# Revit family: Varmax_525_600_2-3Piquages - depuis 2020-06_FR_#
name_source: partatom
category: Equipement de génie climatique
revit_build: Autodesk Revit 2016 (Build: 20150220_1215(x64)
units: mm (PartAtom-declared; Revit-internal decimal feet)

## family parameters
Basée sur le plan de construction = Non
Cote de connecteur circulaire = Utiliser le diamètre
Couper avec des vides une fois chargée = Non
Numéro OmniClass = 23.75.00.00
Partagée = Non
Point de calcul de pièce = Oui
Titre OmniClass = Climate Control (HVAC)
Toujours verticalement = Oui
Type d'élément = Normal

## types (6) — shared parameters
Classe Nox = 6
Fabricant = Atlantic Guillot
Famille = Chaudière collective sol gaz
Fréquence = 50 Hz
Garantie autres pièces = 2 ans
Garantie corps de chauffe = 3 ans
Hauteur = 2016 mm  [stored 6.61417 ft]
Hauteur chaudière (hors pieds) = 2016 mm  [stored 6.61417 ft]
Hauteur de pieds mini = 45 mm
Hauteur entrée d’air (hors pieds) = 1851.5 mm  [stored 6.07448 ft]
Hauteur piquage départ (hors pieds) = 1778 mm  [stored 5.83333 ft]
Hauteur piquage gaz (hors pieds) = 1555 mm  [stored 5.10171 ft]
Hauteur piquage retour chaud (hors pieds) = 1402 mm  [stored 4.59974 ft]
Largeur = 1161 mm  [stored 3.80906 ft]
Largeur chaudière avec jaquette = 1161 mm  [stored 3.80906 ft]
Lien données RT (Edibatec) = http://www.edibatec.org
Lien page produit = https://www.atlantic-solutions-chaufferie.fr
Lien pièces détachées = https://www.atlantic-solutions-chaufferie.fr
Longueur piquages départ / retour = 208 mm
Marque3D = Oui
Matériau corps de chauffe = Acier inoxydable
Nombre piquages = 3
Poids à vide = 800 kg
Pression de service = 6 bar
Profondeur = 1588 mm  [stored 5.20997 ft]
Profondeur chaudière = 1588 mm  [stored 5.20997 ft]
Raccordement fumées = Cheminée (B23/B23p) / Ventouse (C53)
Réseau (mono/tri) = Monophasé
Taux de modulation = 0.2
Tension d'alimentation = 230 V
Type d'énergie = Gaz naturel
URL = https://www.atlantic-solutions-chaufferie.fr
température de consigne départ maximale = 85 °C
volume en eau = 420 l
Ø nominal 1er retour froid = 100 mm  [stored 0.328084 ft]
Ø nominal 2eme retour chaud = 100 mm  [stored 0.328084 ft]
Ø nominal départ = 100 mm  [stored 0.328084 ft]
Ø piquage soupape = 32 mm  [stored 0.104987 ft]
Ø évacuation condensats = 25 mm  [stored 0.082021 ft]
Ø_Entrée d'air = 180 mm  [stored 0.590551 ft]
Ø_Sortie fumées = 200 mm  [stored 0.656168 ft]

## per-type parameters (varying)
| type | Code article | Description | Dia int piquage gaz | Modèle | Pression d'alimentation gaz naturel | Puissance utile nominale à régime 50/30 °C | Puissance utile nominale à régime 80/60 °C | Puissance électrique absorbée à Qn | Référence |
| VARMAX 525 20MB 2/3 PIQUAGES | 541826 | Chaudière sol gaz à condensation en inox 525 kW 2/3 piquages | 54.5 mm  [stored 0.178806 ft] | Varmax 525 | 20 mbar | 558 kW | 513 kW | 697 VA | VARMAX 252 20MB 2-3 PIQUAGES |
| VARMAX 600 20MB 2/3 PIQUAGES | 541830 | Chaudière sol gaz à condensation en inox 600 kW 2/3 piquages | 54.5 mm  [stored 0.178806 ft] | Varmax 600 | 20 mbar | 637 kW | 586 kW | 960 VA | VARMAX 600 20MB 2-3 PIQUAGES |
| VARMAX 600 300MB 2/3 PIQUAGES | 541831 | Chaudière sol gaz à condensation en inox 600 kW 2/3 piquages | 36.6 mm | Varmax 600 | 300 mbar | 637 kW | 586 kW | 960 VA | VARMAX 600 300MB 2-3 PIQUAGES |
| VARMAX 525 300MB 2/3 PIQUAGES | 541827 | Chaudière sol gaz à condensation en inox 252 kW 2/3 piquages | 36.6 mm | Varmax 525 | 300 mbar | 558 kW | 513 kW | 697 VA | VARMAX 525 300MB 2-3 PIQUAGES |
| VARMAX 499 20MB 2/3 PIQUAGES | 541830 | Chaudière sol gaz à condensation en inox 600 kW 2/3 piquages | 54.5 mm  [stored 0.178806 ft] | Varmax 600 | 20 mbar | 530 kW | 488 kW | 612 VA | VARMAX 600 20MB 2-3 PIQUAGES |
| VARMAX 499 300MB 2/3 PIQUAGES | 541830 | Chaudière sol gaz à condensation en inox 600 kW 2/3 piquages | 36.6 mm | Varmax 600 | 300 mbar | 530 kW | 488 kW | 612 VA | VARMAX 600 20MB 2-3 PIQUAGES |

note: [stored X ft] marks values corroborated as IEEE doubles in the binary element streams (Revit-internal decimal feet)

## geometry (parser evidence)
native form markers: Sweep x1
no freeform markers — native parametric forms only
